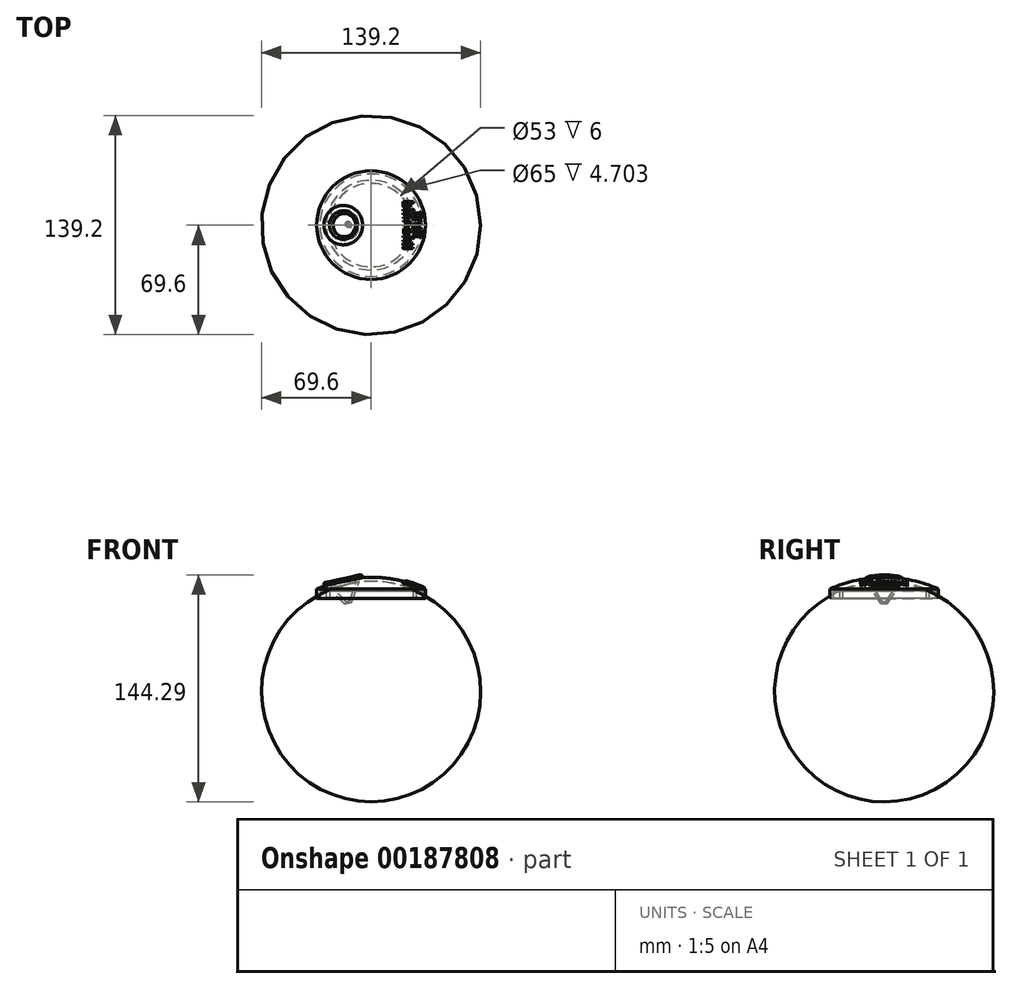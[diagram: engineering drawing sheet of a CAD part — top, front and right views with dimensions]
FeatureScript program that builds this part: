
annotation { "Feature Type Name" : "Feature", "Feature Type Description" : "" }
export const myFeature = defineFeature(function(context is Context, id is Id, definition is map)
    precondition{}
    {
        {
            var Q0;
            Q0=qCreatedBy(makeId("Front.planeOp"),FACE);
            var sketch = newSketch(context, id + "F0", { "sketchPlane" : qUnion([Q0])});
            skLineSegment(sketch, "E0", {"start": v(-26.5, 0) * mm, "end": v(-26.5, -6) * mm});
            skLineSegment(sketch, "E1", {"start": v(-26.5, -6) * mm, "end": v(-28.5, -6) * mm});
            skLineSegment(sketch, "E2", {"start": v(-28.5, -6) * mm, "end": v(-28.5, -1.3) * mm});
            skLineSegment(sketch, "E3", {"start": v(-28.5, -1.3) * mm, "end": v(-32.5, -1.3) * mm});
            skLineSegment(sketch, "E4", {"start": v(-32.5, -1.3) * mm, "end": v(-32.5, -6) * mm});
            skLineSegment(sketch, "E5", {"start": v(-32.5, -6) * mm, "end": v(-34.5, -6) * mm});
            skLineSegment(sketch, "E6", {"start": v(-34.5, -6) * mm, "end": v(-34.5, 0) * mm});
            skLineSegment(sketch, "E7", {"start": v(0, 0) * mm, "end": v(0, 7.5) * mm, "construction": true});
            skArc(sketch, "E8", {"start": v(0, 5) * mm, "mid": v(-13.5, 3.79) * mm, "end": v(-26.5, 0) * mm});
            skPoint(sketch, "E9.start.orphan", {"position": v(26, 0) * mm});
            skArc(sketch, "E10", {"start": v(0, 7.5) * mm, "mid": v(-17.65, 5.6) * mm, "end": v(-34.5, 0) * mm});
            skCircle(sketch, "E11", {"center": v(-32.5, -1.3) * mm, "radius": 2 * mm, "construction": true});
            skLineSegment(sketch, "E12", {"start": v(0, 5) * mm, "end": v(0, 7.5) * mm});
            skSolve(sketch);
        }
        {
            var Q0;
            Q0 = qSketchRegion(id + "F0", true);
            var Q1;
            Q1=sQuery(id+"F0.wireOp",EDGE,"E7");
            revolve(context, id + "F1", {"entities" : qUnion([Q0]), "axis" : qUnion([Q1]), "revolveType" : RevolveType.FULL});
        }
        {
            var Q0;
            Q0=qCreatedBy(makeId("Front.planeOp"),FACE);
            var sketch = newSketch(context, id + "F2", { "sketchPlane" : qUnion([Q0])});
            skLineSegment(sketch, "E13", {"start": v(-18, 6.6) * mm, "end": v(-14.8, -8.05) * mm, "construction": true});
            skLineSegment(sketch, "E14", {"start": v(-14.8, -8.05) * mm, "end": v(-15.96, -8.3) * mm, "construction": true});
            skLineSegment(sketch, "E15", {"start": v(-15.96, -8.3) * mm, "end": v(-27.77, 4.47) * mm});
            skLineSegment(sketch, "E16", {"start": v(-27.77, 4.47) * mm, "end": v(-18, 6.6) * mm, "construction": true});
            skLineSegment(sketch, "E17", {"start": v(-15.96, -8.3) * mm, "end": v(-15.75, -9.28) * mm});
            skLineSegment(sketch, "E18", {"start": v(-15.75, -9.28) * mm, "end": v(-16.73, -9.5) * mm});
            skLineSegment(sketch, "E19", {"start": v(-16.73, -9.5) * mm, "end": v(-30.21, 3.93) * mm, "construction": true});
            skLineSegment(sketch, "E20", {"start": v(-30.21, 3.93) * mm, "end": v(-27.77, 4.47) * mm});
            skArc(sketch, "E21", {"start": v(34.91, -0.19) * mm, "mid": v(17.87, 5.55) * mm, "end": v(0, 7.5) * mm, "construction": true});
            skLineSegment(sketch, "E22", {"start": v(-30.21, 3.93) * mm, "end": v(-29.78, 1.98) * mm});
            skArc(sketch, "E23", {"start": v(-27.61, 1.35) * mm, "mid": v(-28.62, 1.94) * mm, "end": v(-29.78, 1.98) * mm});
            skLineSegment(sketch, "E24", {"start": v(-16.73, -9.5) * mm, "end": v(-27.61, 1.35) * mm});
            skLineSegment(sketch, "E25", {"start": v(0, 0) * mm, "end": v(0, 7.5) * mm, "construction": true});
            skArc(sketch, "E26", {"start": v(0, 7.5) * mm, "mid": v(-17.41, 5.66) * mm, "end": v(-34.05, 0.2) * mm, "construction": true});
            skSolve(sketch);
        }
        {
            var Q0;
            Q0 = qSketchRegion(id + "F2", true);
            var Q1;
            Q1=sQuery(id+"F2.wireOp",EDGE,"E13");
            revolve(context, id + "F3", {"operationType" : NewBodyOperationType.ADD, "entities" : qUnion([Q0]), "axis" : qUnion([Q1]), "revolveType" : RevolveType.FULL});
        }
        {
            var Q0;
            Q0=qCreatedBy(makeId("Front.planeOp"),FACE);
            var sketch = newSketch(context, id + "F4", { "sketchPlane" : qUnion([Q0])});
            skLineSegment(sketch, "E27", {"start": v(-18, 6.6) * mm, "end": v(-14.8, -8.05) * mm, "construction": true});
            skLineSegment(sketch, "E28", {"start": v(-14.8, -8.05) * mm, "end": v(-15.28, -8.15) * mm, "construction": true});
            skLineSegment(sketch, "E29", {"start": v(-15.28, -8.15) * mm, "end": v(-27.77, 4.47) * mm});
            skLineSegment(sketch, "E30", {"start": v(-27.77, 4.47) * mm, "end": v(-18, 6.6) * mm, "construction": true});
            skLineSegment(sketch, "E31", {"start": v(-15.28, -8.15) * mm, "end": v(-15.07, -9.13) * mm});
            skLineSegment(sketch, "E32", {"start": v(-15.07, -9.13) * mm, "end": v(-16.04, -9.34) * mm, "construction": true});
            skLineSegment(sketch, "E33", {"start": v(-16.04, -9.34) * mm, "end": v(-30.21, 3.93) * mm, "construction": true});
            skLineSegment(sketch, "E34", {"start": v(-30.21, 3.93) * mm, "end": v(-27.77, 4.47) * mm, "construction": true});
            skLineSegment(sketch, "E35", {"start": v(-30.21, 3.93) * mm, "end": v(-29.78, 1.98) * mm, "construction": true});
            skArc(sketch, "E36", {"start": v(-27.44, 1.33) * mm, "mid": v(-28.53, 1.95) * mm, "end": v(-29.78, 1.98) * mm, "construction": true});
            skLineSegment(sketch, "E37", {"start": v(-16.04, -9.34) * mm, "end": v(-27.44, 1.33) * mm, "construction": true});
            skArc(sketch, "E38", {"start": v(34.91, -0.19) * mm, "mid": v(0, 7.5) * mm, "end": v(-34.91, -0.19) * mm});
            skArc(sketch, "E39", {"start": v(34.91, -0.19) * mm, "mid": v(0, 7.5) * mm, "end": v(-34.91, -0.19) * mm, "construction": true});
            skLineSegment(sketch, "E40", {"start": v(-15.07, -9.13) * mm, "end": v(-14.58, -9.02) * mm});
            skLineSegment(sketch, "E41", {"start": v(-14.58, -9.02) * mm, "end": v(-18, 6.6) * mm});
            skLineSegment(sketch, "E42", {"start": v(-18, 6.6) * mm, "end": v(-27.77, 4.47) * mm});
            skSolve(sketch);
        }
        {
            var Q0;
            Q0 = qSketchRegion(id + "F4", true);
            var Q1;
            Q1=sQuery(id+"F4.wireOp",EDGE,"E41");
            revolve(context, id + "F5", {"operationType" : NewBodyOperationType.REMOVE, "entities" : qUnion([Q0]), "axis" : qUnion([Q1]), "revolveType" : RevolveType.FULL, "oppositeDirection" : true});
        }
        {
            var Q0;
            Q0=makeQuery(id+"F3.opRevolve","SWEPT_EDGE",EDGE,{"disambiguationData":[OSD([sQuery(id+"F2.wireOp",EDGE,"E22"),sQuery(id+"F2.wireOp",EDGE,"E23")])]});
            var Q1;
            Q1=makeQuery(id+"F3.opRevolve","SWEPT_EDGE",EDGE,{"disambiguationData":[OSD([sQuery(id+"F2.wireOp",EDGE,"E20"),sQuery(id+"F2.wireOp",EDGE,"E22")])]});
            var Q2;
            Q2=makeQuery(id+"F3.opRevolve","SWEPT_EDGE",EDGE,{"disambiguationData":[OSD([sQuery(id+"F2.wireOp",EDGE,"E15"),sQuery(id+"F2.wireOp",EDGE,"E20")])]});
            var Q3;
            Q3=makeQuery(id+"FBX9GPGToqFceus_1.1.F3.opRevolve","SWEPT_EDGE",EDGE,{"disambiguationData":[OSD([sQuery(id+"F2.wireOp",EDGE,"E22"),sQuery(id+"F2.wireOp",EDGE,"E23")])]});
            var Q4;
            Q4=makeQuery(id+"FBX9GPGToqFceus_1.1.F3.opRevolve","SWEPT_EDGE",EDGE,{"disambiguationData":[OSD([sQuery(id+"F2.wireOp",EDGE,"E20"),sQuery(id+"F2.wireOp",EDGE,"E22")])]});
            var Q5;
            Q5=makeQuery(id+"FBX9GPGToqFceus_1.2.F3.opRevolve","SWEPT_EDGE",EDGE,{"disambiguationData":[OSD([sQuery(id+"F2.wireOp",EDGE,"E22"),sQuery(id+"F2.wireOp",EDGE,"E23")])]});
            var Q6;
            Q6=makeQuery(id+"FBX9GPGToqFceus_1.2.F3.opRevolve","SWEPT_EDGE",EDGE,{"disambiguationData":[OSD([sQuery(id+"F2.wireOp",EDGE,"E20"),sQuery(id+"F2.wireOp",EDGE,"E22")])]});
            var Q7;
            Q7=makeQuery(id+"FBX9GPGToqFceus_1.1.F3.opRevolve","SWEPT_EDGE",EDGE,{"disambiguationData":[OSD([sQuery(id+"F2.wireOp",EDGE,"E15"),sQuery(id+"F2.wireOp",EDGE,"E20")])]});
            var Q8;
            Q8=makeQuery(id+"FBX9GPGToqFceus_1.2.F3.opRevolve","SWEPT_EDGE",EDGE,{"disambiguationData":[OSD([sQuery(id+"F2.wireOp",EDGE,"E15"),sQuery(id+"F2.wireOp",EDGE,"E20")])]});
            fillet(context, id + "F6", {"entities" : qUnion([Q0, Q1, Q2, Q3, Q4, Q5, Q6, Q7, Q8]), "radius" : 1 * mm, "tangentPropagation" : true, "allowEdgeOverflow" : false});
        }
        {
            var Q0;
            Q0=qCreatedBy(makeId("Front.planeOp"),FACE);
            var sketch = newSketch(context, id + "F7", { "sketchPlane" : qUnion([Q0])});
            skArc(sketch, "E43", {"start": v(34.5, 0) * mm, "mid": v(-0.23, 7.5) * mm, "end": v(-34.91, -0.19) * mm});
            skArc(sketch, "E44", {"start": v(34.5, 0) * mm, "mid": v(-0.23, 7.5) * mm, "end": v(-34.91, -0.19) * mm, "construction": true});
            skLineSegment(sketch, "E45", {"start": v(19.61, 5.15) * mm, "end": v(21.98, 14.92) * mm, "construction": true});
            skLineSegment(sketch, "E46", {"start": v(34.5, 0) * mm, "end": v(38.86, 9.55) * mm, "construction": true});
            skLineSegment(sketch, "E47.0", {"start": v(34.5, 0) * mm, "end": v(-34.5, 0) * mm});
            skLineSegment(sketch, "E48", {"start": v(21.7, 13.71) * mm, "end": v(38.86, 9.55) * mm});
            skSolve(sketch);
        }
        {
            var Q0;
            Q0=qCreatedBy(makeId("Top.planeOp"),FACE);
            var Q1;
            Q1=sQuery(id+"F7.wireOp",VERTEX,"E45.start");
            cPlane(context, id + "F8", {"entities" : qUnion([Q0, Q1]), "cplaneType" : CPlaneType.PLANE_POINT, "offset" : 0 * mm, "width" : 150 * mm, "height" : 150 * mm});
        }
        {
            var Q0;
            Q0=qCreatedBy(id+"F8.planeOp",FACE);
            var sketch = newSketch(context, id + "F9", { "sketchPlane" : qUnion([Q0])});
            skPoint(sketch, "E49.0", {"position": v(21.98, 0) * mm});
            skLineSegment(sketch, "E50", {"start": v(21.98, 0) * mm, "end": v(21.98, -48.11) * mm});
            skSolve(sketch);
        }
        {
            var Q0;
            Q0=sQuery(id+"F9.wireOp",VERTEX,"E49.0");
            var Q1;
            Q1=sQuery(id+"F7.wireOp",VERTEX,"E48.end");
            var Q2;
            Q2=sQuery(id+"F9.wireOp",VERTEX,"E50.end");
            cPlane(context, id + "F10", {"entities" : qUnion([Q0, Q1, Q2]), "cplaneType" : CPlaneType.THREE_POINT, "offset" : 25 * mm, "width" : 150 * mm, "height" : 150 * mm});
        }
        {
            var Q0;
            Q0=qCreatedBy(id+"F10.planeOp",FACE);
            var sketch = newSketch(context, id + "F11", { "sketchPlane" : qUnion([Q0])});
            skLineSegment(sketch, "E51", {"start": v(0, 0) * mm, "end": v(34.12, 0) * mm, "construction": true});
            skText(sketch, "E52", { "text": "fruit", "fontName": "AllertaStencil-Regular.ttf"});
            skText(sketch, "E53", { "text": "binnen!!", "fontName": "AllertaStencil-Regular.ttf"});
            skEllipse(sketch, "E54.0", {"center": v(6.98, -15.2) * mm, "majorRadius": 13.34 * mm, "minorRadius": 13.01 * mm, "majorAxis": v(0.69, -0.72), "construction": true});
            skEllipse(sketch, "E55.0", {"center": v(0, 0) * mm, "majorRadius": 35 * mm, "minorRadius": 34.01 * mm, "majorAxis": v(0, -1), "construction": true});
            skCircle(sketch, "E56", {"center": v(31.05, 8.63) * mm, "radius": 0.75 * mm, "construction": true});
            const initialGuessF11  = {"E52": [0.02659, 0.00863, 0, -1, 0.0056], "E53": [0.02067, 0.01548, 0, -1, 0.0056]};
            skSetInitialGuess(sketch, initialGuessF11);
            skSolve(sketch);
        }
        {
            var Q0;
            Q0 = qSketchRegion(id + "F11", true);
            extrude(context, id + "F12", {"entities" : qUnion([Q0]), "endBound" : BoundingType.UP_TO_NEXT, "oppositeDirection" : true, "depth" : 25 * mm});
        }
        {
            var Q0;
            Q0=qCreatedBy(makeId("Front.planeOp"),FACE);
            var sketch = newSketch(context, id + "F13", { "sketchPlane" : qUnion([Q0])});
            skArc(sketch, "E57", {"start": v(34.81, 0.68) * mm, "mid": v(28.18, 3.37) * mm, "end": v(21.35, 5.49) * mm});
            skLineSegment(sketch, "E58", {"start": v(21.35, 5.49) * mm, "end": v(18.7, 15.45) * mm});
            skLineSegment(sketch, "E59", {"start": v(18.7, 15.45) * mm, "end": v(43.8, 9.5) * mm});
            skLineSegment(sketch, "E60", {"start": v(43.8, 9.5) * mm, "end": v(34.81, 0.68) * mm});
            skSolve(sketch);
        }
        {
            var Q0;
            Q0=makeQuery(id+"F13.imprint","IMPRINT",FACE,{"disambiguationData":[TD([[makeQuery(id+"F13.imprint","IMPRINT",EDGE,{"derivedFrom":sQuery(id+"F13.wireOp",EDGE,"E57")}),-1.0]])]});
            extrude(context, id + "F14", {"entities" : qUnion([Q0]), "operationType" : NewBodyOperationType.REMOVE, "depth" : 43 * mm, "symmetric" : true});
        }
    });
